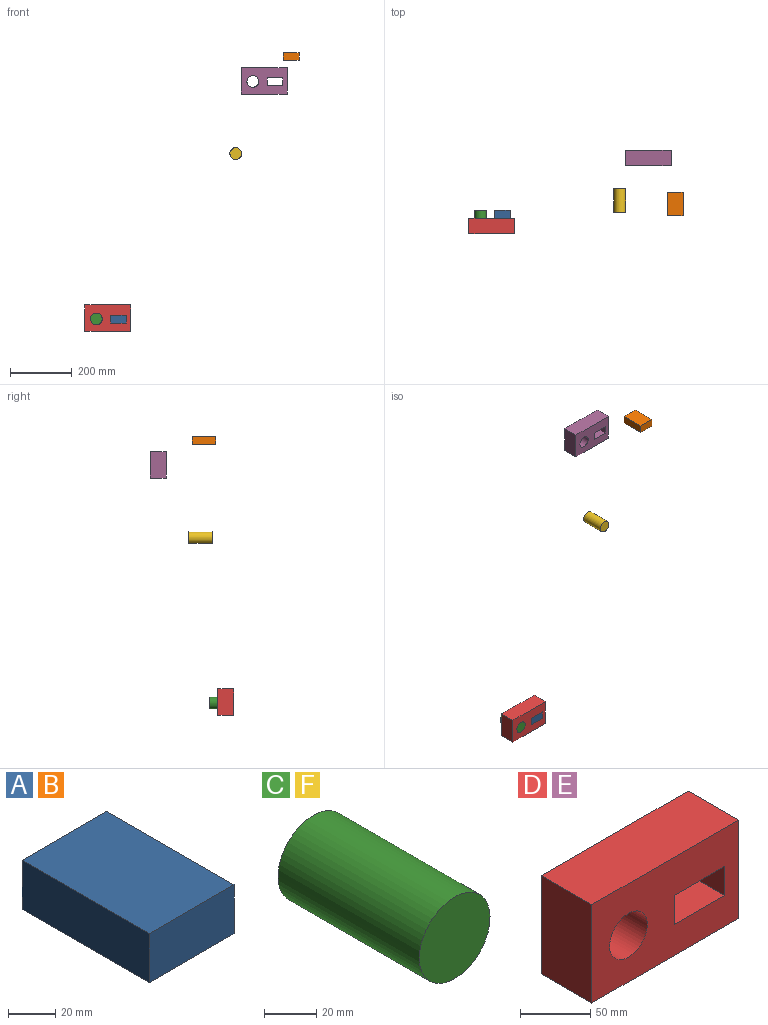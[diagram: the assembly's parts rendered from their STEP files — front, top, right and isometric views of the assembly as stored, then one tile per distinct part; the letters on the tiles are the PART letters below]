
ASSEMBLY  parts=6 mates=4
PART A: 6 faces, bbox 50.8x76.2x25.4 mm
  f0: plane 76.2x50.8mm, normal (0,0,1), area 3871mm2, adj f1,f3,f4,f5
  f1: plane 76.2x25.4mm, normal (-1,0,0), area 1935.5mm2, adj f0,f2,f4,f5
  f2: plane 76.2x50.8mm, normal (0,0,-1), area 3871mm2, adj f1,f3,f4,f5
  f3: plane 76.2x25.4mm, normal (1,0,0), area 1935.5mm2, adj f0,f2,f4,f5
  f4: plane 50.8x25.4mm, normal (0,-1,0), area 1290.3mm2, adj f0,f1,f2,f3
  f5: plane 50.8x25.4mm, normal (0,1,0), area 1290.3mm2, adj f0,f1,f2,f3
PART B: same geometry as A
PART C: 3 faces, bbox 38.1x76.2x38.1 mm
  f0: cylinder r=19.05mm len=76.2mm, axis (0,1,0), area 9120.7mm2, adj f1,f2
  f1: plane 38.1x38.1mm, normal (0,-1,0), area 1140.1mm2, adj f0
  f2: plane 38.1x38.1mm, normal (0,1,0), area 1140.1mm2, adj f0
PART D: 11 faces, bbox 147.9x50.8x85.8 mm
  f0: plane 147.89x50.8mm, normal (0,0,1), area 7512.8mm2, adj f1,f8,f9,f10
  f1: plane 85.82x50.8mm, normal (-1,0,0), area 4359.9mm2, adj f0,f2,f9,f10
  f2: plane 147.89x50.8mm, normal (0,0,-1), area 7512.8mm2, adj f1,f8,f9,f10
  f3: plane 50.8x25.4mm, normal (1,0,0), area 1290.3mm2, adj f4,f6,f9,f10
  f4: plane 50.8x50.8mm, normal (0,0,-1), area 2580.6mm2, adj f3,f5,f9,f10
  f5: plane 50.8x25.4mm, normal (-1,0,0), area 1290.3mm2, adj f4,f6,f9,f10
  f6: plane 50.8x50.8mm, normal (0,0,1), area 2580.6mm2, adj f3,f5,f9,f10
  f7: cylinder r=19.05mm len=50.8mm, axis (0,1,0), area 6080.5mm2, adj f9,f10
  f8: plane 85.82x50.8mm, normal (1,0,0), area 4359.9mm2, adj f0,f2,f9,f10
  f9: plane 147.89x85.82mm, normal (0,-1,0), area 10262.1mm2, adj f0,f1,f2,f3,f4,f5,f6,f7
  f10: plane 147.89x85.82mm, normal (0,1,0), area 10262.1mm2, adj f0,f1,f2,f3,f4,f5,f6,f7
PART E: same geometry as D
PART F: same geometry as C
PLACE A rot(axis=(1,0,0),180deg) t=(79.27,-24.53,1.17)mm
PLACE B t=(638.71,108.95,730.99)mm
PLACE C t=(-59.4,51.67,-107.96)mm
PLACE D t=(-10.99,26.27,-79.91)mm
PLACE E t=(495.53,244.37,688.36)mm
PLACE F t=(391.84,120.28,426.88)mm
MATE fastened D.f9 <-> A.f5  axis (0,-1,0) through (36.8,-24.53,-71.63)mm
MATE fastened A.f0 <-> D.f6  axis (0,0,-1) through (36.8,13.57,-71.63)mm
MATE fastened C.f0 <-> D.f7  axis (0,-1,0) through (-34.55,-24.53,-58.09)mm
MATE fastened A.f4 <-> D.f9  axis (0,1,0) through (36.8,51.67,-58.93)mm
